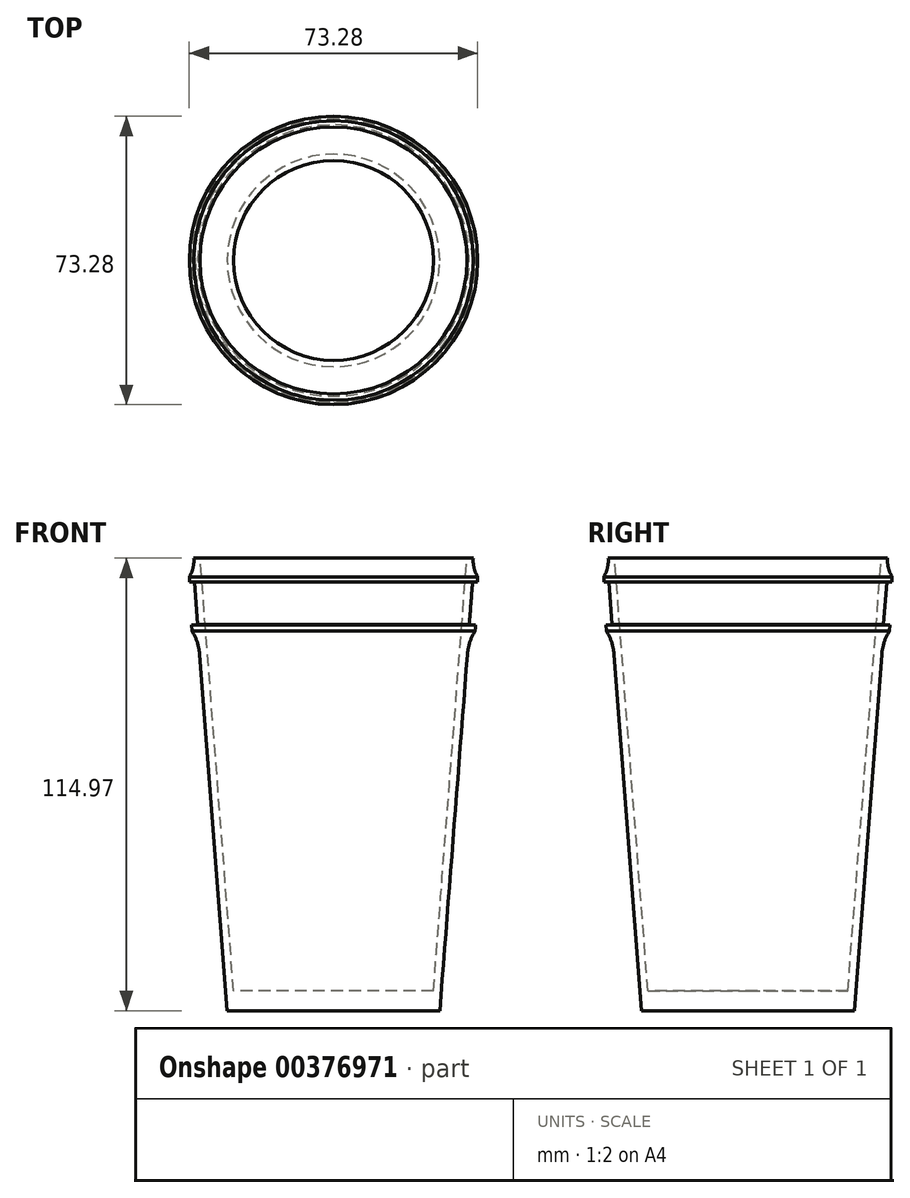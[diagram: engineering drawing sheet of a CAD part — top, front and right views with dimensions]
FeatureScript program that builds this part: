
annotation { "Feature Type Name" : "Feature", "Feature Type Description" : "" }
export const myFeature = defineFeature(function(context is Context, id is Id, definition is map)
    precondition{}
    {
        {
            var Q0;
            Q0=qCreatedBy(makeId("Front.planeOp"),FACE);
            var sketch = newSketch(context, id + "F0", { "sketchPlane" : qUnion([Q0])});
            skLineSegment(sketch, "E0", {"start": v(0, -57.5) * mm, "end": v(27, -57.5) * mm});
            skLineSegment(sketch, "E1", {"start": v(33.9, 57.47) * mm, "end": v(25.38, -52.5) * mm});
            skLineSegment(sketch, "E2", {"start": v(25.38, -52.5) * mm, "end": v(0, -52.5) * mm});
            skLineSegment(sketch, "E3", {"start": v(0, -52.5) * mm, "end": v(0, -57.5) * mm});
            skLineSegment(sketch, "E4", {"start": v(33.9, 57.47) * mm, "end": v(35.5, 57.47) * mm});
            skLineSegment(sketch, "E5", {"start": v(36.54, 51.47) * mm, "end": v(35.33, 51.56) * mm});
            skLineSegment(sketch, "E6", {"start": v(36.54, 51.47) * mm, "end": v(36.64, 52.7) * mm});
            skLineSegment(sketch, "E7", {"start": v(36.64, 52.7) * mm, "end": v(35.14, 52.82) * mm});
            skLineSegment(sketch, "E8", {"start": v(35.14, 52.82) * mm, "end": v(35.5, 57.47) * mm});
            skLineSegment(sketch, "E9", {"start": v(35.33, 51.56) * mm, "end": v(34.48, 40.6) * mm});
            skLineSegment(sketch, "E10", {"start": v(34.48, 40.6) * mm, "end": v(36.1, 40.47) * mm});
            skLineSegment(sketch, "E11", {"start": v(36.1, 40.47) * mm, "end": v(35.98, 38.98) * mm});
            skLineSegment(sketch, "E12", {"start": v(35.98, 38.98) * mm, "end": v(34.48, 39.1) * mm});
            skLineSegment(sketch, "E13", {"start": v(34.48, 39.1) * mm, "end": v(27, -57.5) * mm});
            skSolve(sketch);
        }
        {
            var Q0;
            Q0=qCreatedBy(makeId("Front.planeOp"),FACE);
            var sketch = newSketch(context, id + "F1", { "sketchPlane" : qUnion([Q0])});
            skLineSegment(sketch, "E14", {"start": v(0, 94.12) * mm, "end": v(0, -94.95) * mm});
            skSolve(sketch);
        }
        {
            var Q0;
            Q0 = qSketchRegion(id + "F0", true);
            var Q1;
            Q1=sQuery(id+"F1.wireOp",EDGE,"E14");
            revolve(context, id + "F2", {"entities" : qUnion([Q0]), "axis" : qUnion([Q1]), "revolveType" : RevolveType.FULL});
        }
        {
            var Q0;
            Q0=makeQuery(id+"F2.opRevolve","SWEPT_EDGE",EDGE,{"disambiguationData":[OSD([sQuery(id+"F0.wireOp",EDGE,"E12"),sQuery(id+"F0.wireOp",EDGE,"E13")])]});
            fillet(context, id + "F3", {"entities" : qUnion([Q0]), "radius" : 13 * mm, "tangentPropagation" : true, "allowEdgeOverflow" : false});
        }
        {
            var Q0;
            Q0=makeQuery(id+"F2.opRevolve","SWEPT_EDGE",EDGE,{"disambiguationData":[OSD([sQuery(id+"F0.wireOp",EDGE,"E7"),sQuery(id+"F0.wireOp",EDGE,"E8")])]});
            fillet(context, id + "F4", {"entities" : qUnion([Q0]), "radius" : 8 * mm, "tangentPropagation" : true, "allowEdgeOverflow" : false});
        }
    });
